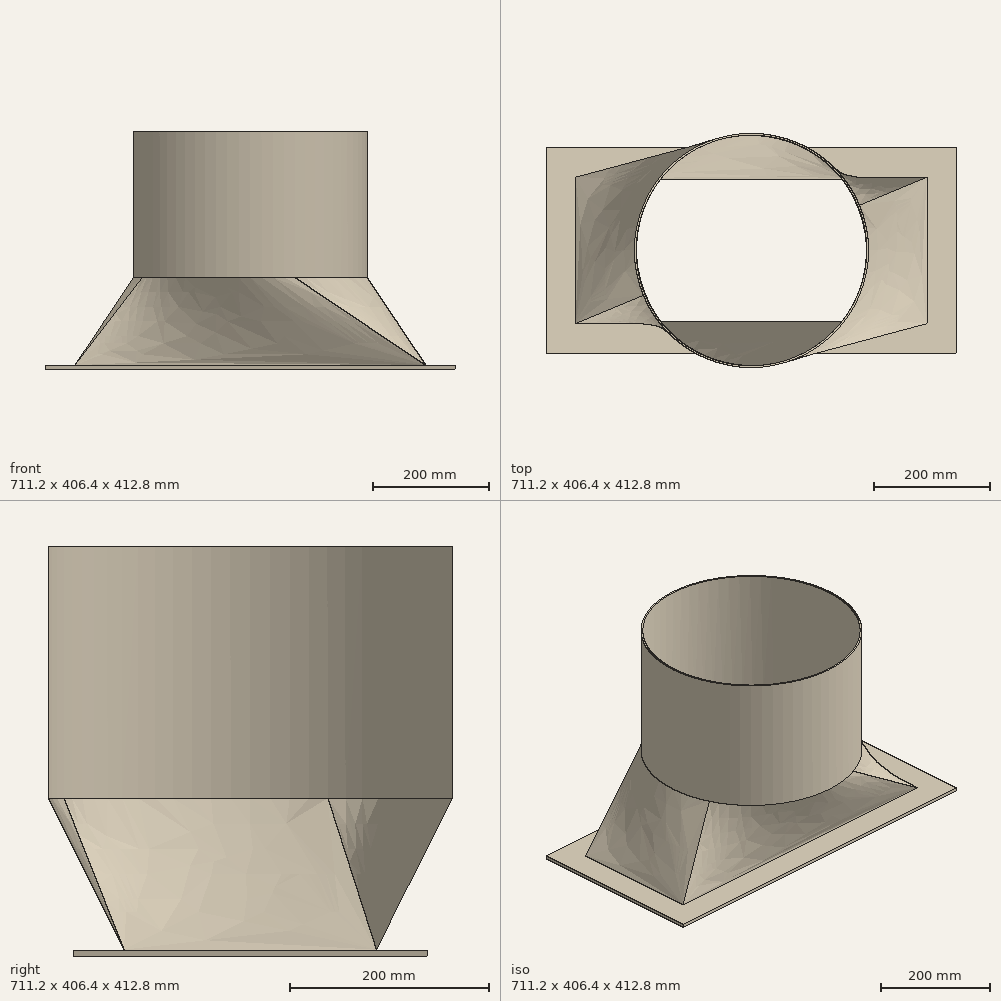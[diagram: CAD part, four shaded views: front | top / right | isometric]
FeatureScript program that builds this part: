
annotation { "Feature Type Name" : "Feature", "Feature Type Description" : "" }
export const myFeature = defineFeature(function(context is Context, id is Id, definition is map)
    precondition{}
    {
        {
            var Q0;
            Q0=qCreatedBy(makeId("Top.planeOp"),FACE);
            var sketch = newSketch(context, id + "F0", { "sketchPlane" : qUnion([Q0])});
            skLineSegment(sketch, "E0.bottom", {"start": v(-304.8, -127) * mm, "end": v(304.8, -127) * mm});
            skLineSegment(sketch, "E0.top", {"start": v(-304.8, 127) * mm, "end": v(304.8, 127) * mm});
            skLineSegment(sketch, "E0.left", {"start": v(-304.8, -127) * mm, "end": v(-304.8, 127) * mm});
            skLineSegment(sketch, "E0.right", {"start": v(304.8, -127) * mm, "end": v(304.8, 127) * mm});
            skPoint(sketch, "E0.middle", {"position": v(0, 0) * mm});
            skSolve(sketch);
        }
        {
            var Q0;
            Q0=qCreatedBy(makeId("Front.planeOp"),FACE);
            var sketch = newSketch(context, id + "F1", { "sketchPlane" : qUnion([Q0])});
            skLineSegment(sketch, "E1", {"start": v(0, 0) * mm, "end": v(0, 152.4) * mm, "construction": true});
            skLineSegment(sketch, "E2", {"start": v(0, 152.4) * mm, "end": v(-304.8, 152.4) * mm, "construction": true});
            skSolve(sketch);
        }
        {
            var Q0;
            Q0=sQuery(id+"F1.wireOp",EDGE,"E2");
            cPlane(context, id + "F2", {"entities" : qUnion([Q0]), "cplaneType" : CPlaneType.LINE_ANGLE, "offset" : 25.4 * mm, "angle" : 90 * degree, "width" : 152.4 * mm, "height" : 152.4 * mm});
        }
        {
            var Q0;
            Q0=qCreatedBy(id+"F2.planeOp",FACE);
            var sketch = newSketch(context, id + "F3", { "sketchPlane" : qUnion([Q0])});
            skCircle(sketch, "E3", {"center": v(0, 0) * mm, "radius": 203.2 * mm});
            skSolve(sketch);
        }
        {
            var Q0;
            Q0=makeQuery(id+"F0.imprint","IMPRINT",FACE,{"disambiguationData":[TD([[makeQuery(id+"F0.imprint","IMPRINT",EDGE,{"derivedFrom":sQuery(id+"F0.wireOp",EDGE,"E0.bottom")}),1.0]])]});
            var Q1;
            Q1=makeQuery(id+"F3.imprint","IMPRINT",FACE,{"disambiguationData":[TD([[makeQuery(id+"F3.imprint","IMPRINT",EDGE,{"derivedFrom":sQuery(id+"F3.wireOp",EDGE,"E3")}),1.0]])]});
            var Q2;
            Q2=sQuery(id+"F3.wireOp",EDGE,"E3");
            var Q3;
            Q3=makeQuery(id+"F0.imprint","IMPRINT",FACE,{"disambiguationData":[TD([[makeQuery(id+"F0.imprint","IMPRINT",EDGE,{"derivedFrom":sQuery(id+"F0.wireOp",EDGE,"E0.bottom")}),1.0]])]});
            loft(context, id + "F4", {"sheetProfilesArray" : [{ "sheetProfileEntities" : qUnion([Q0]) }, { "sheetProfileEntities" : qUnion([Q1]) }], "wireProfilesArray" : [{ "wireProfileEntities" : qUnion([Q2]) }, { "wireProfileEntities" : qUnion([Q3]) }]});
        }
        {
            var Q0;
            Q0=qCreatedBy(id+"F2.planeOp",FACE);
            var sketch = newSketch(context, id + "F5", { "sketchPlane" : qUnion([Q0])});
            skCircle(sketch, "E4", {"center": v(0, 0) * mm, "radius": 203.2 * mm});
            skCircle(sketch, "E5", {"center": v(0, 0) * mm, "radius": 200.03 * mm});
            skSolve(sketch);
        }
        {
            var Q0;
            Q0=makeQuery(id+"F4.opLoft","CAP_FACE",FACE,{"disambiguationData":[OSD([makeQuery(id+"F3.imprint","IMPRINT",FACE,{"disambiguationData":[TD([[makeQuery(id+"F3.imprint","IMPRINT",EDGE,{"derivedFrom":sQuery(id+"F3.wireOp",EDGE,"E3")}),1.0]])]})])],"isStart":true});
            var Q1;
            Q1=makeQuery(id+"F4.opLoft","CAP_FACE",FACE,{"disambiguationData":[OSD([makeQuery(id+"F0.imprint","IMPRINT",FACE,{"disambiguationData":[TD([[makeQuery(id+"F0.imprint","IMPRINT",EDGE,{"derivedFrom":sQuery(id+"F0.wireOp",EDGE,"E0.bottom")}),1.0]])]})])],"isStart":true});
            shell(context, id + "F6", {"entities" : qUnion([Q0, Q1]), "thickness" : 3.17 * mm});
        }
        {
            var Q0;
            Q0=makeQuery(id+"F5.imprint","IMPRINT",FACE,{"disambiguationData":[TD([[makeQuery(id+"F5.imprint","IMPRINT",EDGE,{"derivedFrom":sQuery(id+"F5.wireOp",EDGE,"E4")}),1.0]])]});
            extrude(context, id + "F7", {"entities" : qUnion([Q0]), "operationType" : NewBodyOperationType.ADD, "depth" : 254 * mm, "offsetDistance" : 25.4 * mm});
        }
        {
            var Q0;
            Q0=makeQuery(id+"F0.imprint","IMPRINT",FACE,{"disambiguationData":[TD([[makeQuery(id+"F0.imprint","IMPRINT",EDGE,{"derivedFrom":sQuery(id+"F0.wireOp",EDGE,"E0.bottom")}),1.0]])]});
            var sketch = newSketch(context, id + "F8", { "sketchPlane" : qUnion([Q0])});
            skLineSegment(sketch, "E6.bottom", {"start": v(301.63, 123.83) * mm, "end": v(-301.63, 123.83) * mm});
            skLineSegment(sketch, "E6.top", {"start": v(301.63, -123.83) * mm, "end": v(-301.63, -123.83) * mm});
            skLineSegment(sketch, "E6.left", {"start": v(301.63, 123.83) * mm, "end": v(301.63, -123.83) * mm});
            skLineSegment(sketch, "E6.right", {"start": v(-301.63, 123.83) * mm, "end": v(-301.63, -123.83) * mm});
            skPoint(sketch, "E6.middle", {"position": v(0, 0) * mm});
            skLineSegment(sketch, "E7.bottom", {"start": v(355.6, 177.8) * mm, "end": v(-355.6, 177.8) * mm});
            skLineSegment(sketch, "E7.top", {"start": v(355.6, -177.8) * mm, "end": v(-355.6, -177.8) * mm});
            skLineSegment(sketch, "E7.left", {"start": v(355.6, 177.8) * mm, "end": v(355.6, -177.8) * mm});
            skLineSegment(sketch, "E7.right", {"start": v(-355.6, 177.8) * mm, "end": v(-355.6, -177.8) * mm});
            skSolve(sketch);
        }
        {
            var Q0;
            Q0 = qSketchRegion(id + "F8", true);
            extrude(context, id + "F9", {"entities" : qUnion([Q0]), "operationType" : NewBodyOperationType.ADD, "oppositeDirection" : true, "depth" : 6.35 * mm, "offsetDistance" : 25.4 * mm});
        }
    });
